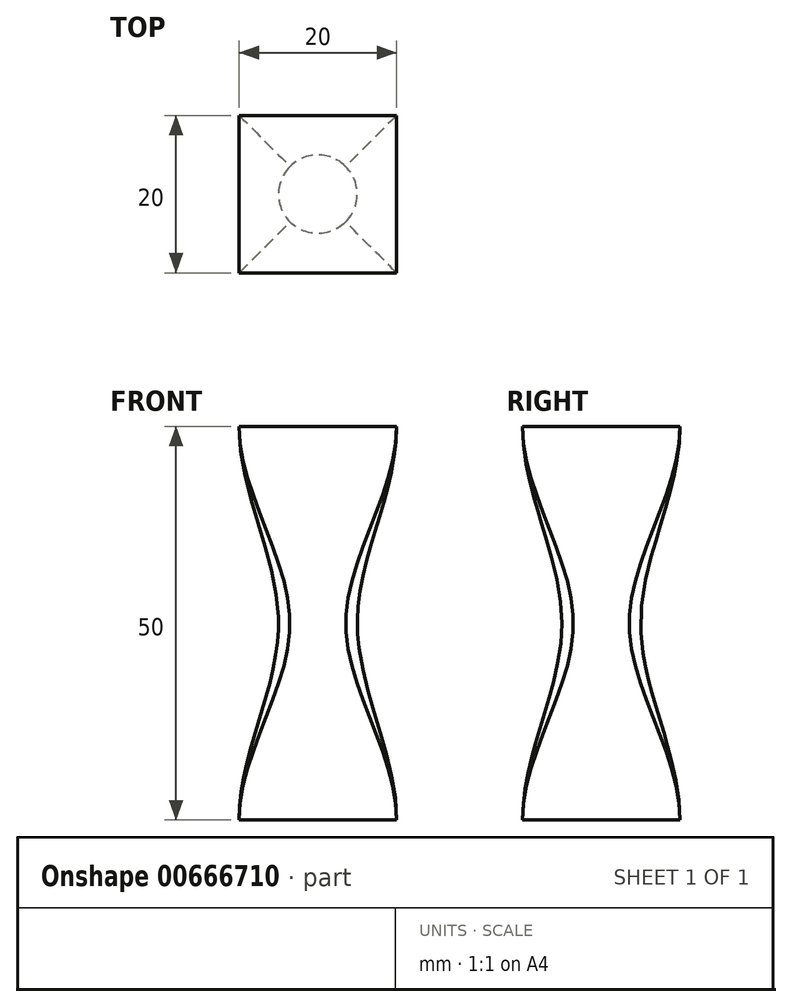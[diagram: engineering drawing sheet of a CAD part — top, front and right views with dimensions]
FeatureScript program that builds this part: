
annotation { "Feature Type Name" : "Feature", "Feature Type Description" : "" }
export const myFeature = defineFeature(function(context is Context, id is Id, definition is map)
    precondition{}
    {
        {
            var Q0;
            Q0=qCreatedBy(makeId("Top.planeOp"),FACE);
            var sketch = newSketch(context, id + "F0", { "sketchPlane" : qUnion([Q0])});
            skLineSegment(sketch, "E0.bottom", {"start": v(-10, -10) * mm, "end": v(10, -10) * mm});
            skLineSegment(sketch, "E0.top", {"start": v(-10, 10) * mm, "end": v(10, 10) * mm});
            skLineSegment(sketch, "E0.left", {"start": v(-10, -10) * mm, "end": v(-10, 10) * mm});
            skLineSegment(sketch, "E0.right", {"start": v(10, -10) * mm, "end": v(10, 10) * mm});
            skPoint(sketch, "E0.middle", {"position": v(0, 0) * mm});
            skSolve(sketch);
        }
        {
            var Q0;
            Q0=qCreatedBy(makeId("Top.planeOp"),FACE);
            cPlane(context, id + "F1", {"entities" : qUnion([Q0]), "cplaneType" : CPlaneType.OFFSET, "offset" : 25 * mm, "oppositeDirection" : true, "width" : 150 * mm, "height" : 150 * mm});
        }
        {
            var Q0;
            Q0=qCreatedBy(id+"F1.planeOp",FACE);
            var sketch = newSketch(context, id + "F2", { "sketchPlane" : qUnion([Q0])});
            skCircle(sketch, "E1", {"center": v(0, 0) * mm, "radius": 5 * mm});
            skSolve(sketch);
        }
        {
            var Q0;
            Q0=qCreatedBy(makeId("Top.planeOp"),FACE);
            cPlane(context, id + "F3", {"entities" : qUnion([Q0]), "cplaneType" : CPlaneType.OFFSET, "offset" : 50 * mm, "oppositeDirection" : true, "width" : 150 * mm, "height" : 150 * mm});
        }
        {
            var Q0;
            Q0=qCreatedBy(id+"F3.planeOp",FACE);
            var sketch = newSketch(context, id + "F4", { "sketchPlane" : qUnion([Q0])});
            skLineSegment(sketch, "E2.0.0", {"start": v(10, 10) * mm, "end": v(-10, 10) * mm});
            skLineSegment(sketch, "E2.0.1", {"start": v(-10, 10) * mm, "end": v(-10, -10) * mm});
            skLineSegment(sketch, "E2.0.2", {"start": v(-10, -10) * mm, "end": v(10, -10) * mm});
            skLineSegment(sketch, "E2.0.3", {"start": v(10, -10) * mm, "end": v(10, 10) * mm});
            skSolve(sketch);
        }
        {
            var Q0;
            Q0 = qSketchRegion(id + "F0", true);
            var Q1;
            Q1 = qSketchRegion(id + "F2", true);
            var Q2;
            Q2 = qSketchRegion(id + "F4", true);
            loft(context, id + "F5", {"startCondition" : LoftEndDerivativeType.NORMAL_TO_PROFILE, "startMagnitude" : 1, "endCondition" : LoftEndDerivativeType.NORMAL_TO_PROFILE, "endMagnitude" : 1, "sheetProfilesArray" : [{ "sheetProfileEntities" : qUnion([Q0]) }, { "sheetProfileEntities" : qUnion([Q1]) }, { "sheetProfileEntities" : qUnion([Q2]) }]});
        }
    });
